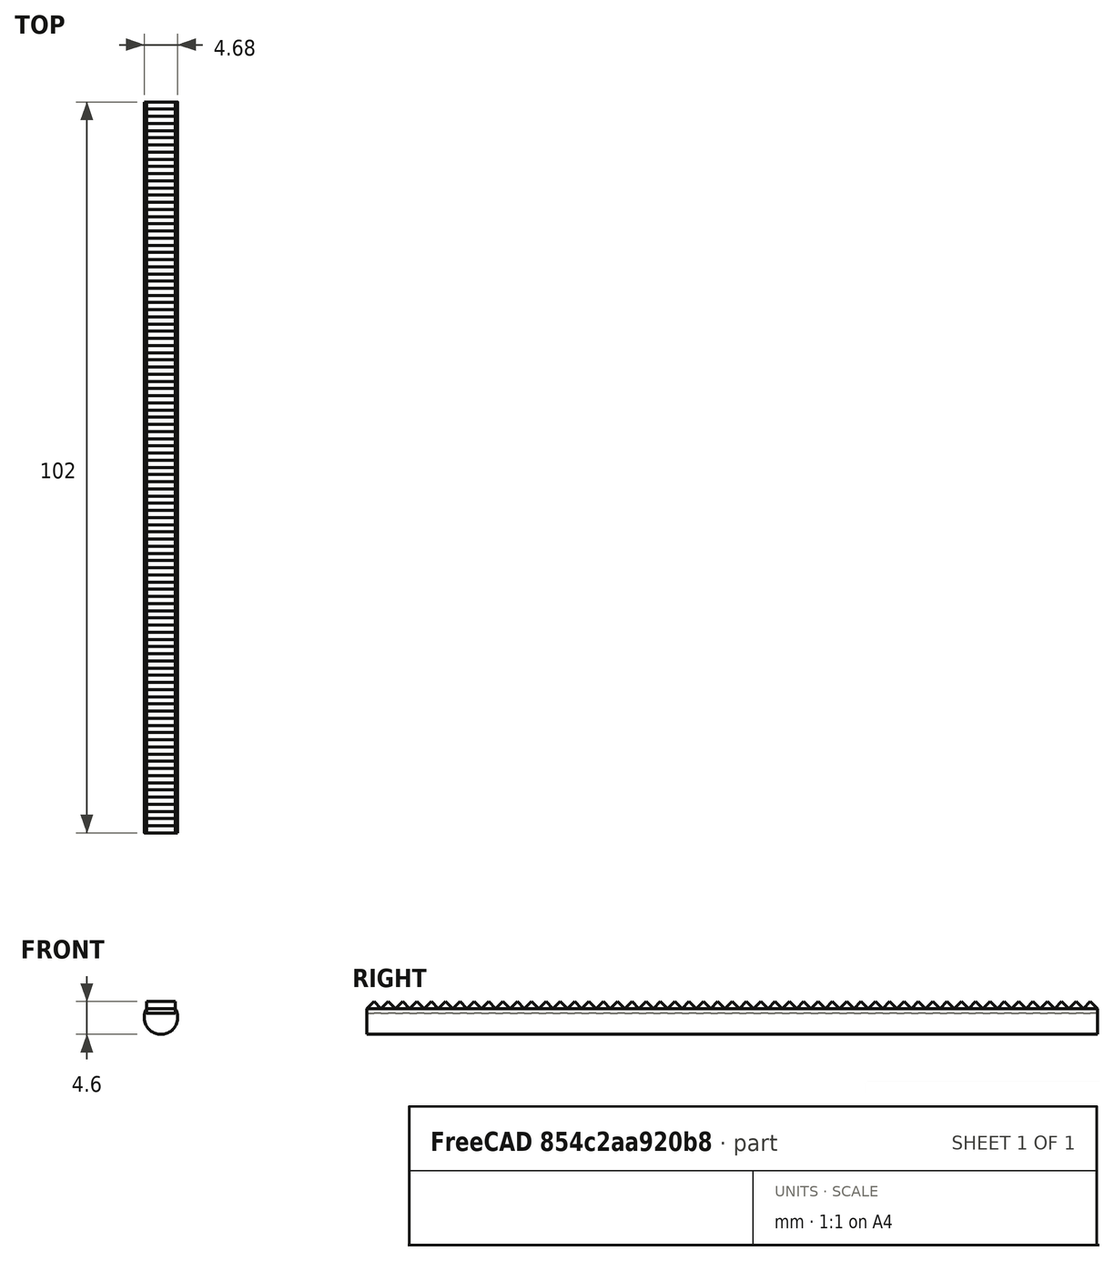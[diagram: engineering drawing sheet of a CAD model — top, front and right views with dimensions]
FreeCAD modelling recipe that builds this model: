
FCSTD DOCUMENT  (FreeCAD 0.19R)
Label: cremaillere
License: All rights reserved
LicenseURL: http://en.wikipedia.org/wiki/All_rights_reserved
objects: PartDesign::Body×3, Sketcher::SketchObject×2, PartDesign::Pad×2, PartDesign::LinearPattern×1, PartDesign::Boolean×1
note: 11 computed .brp shape members not serialized (recipe doc carries the construction recipe); baked Part::Feature solids carry a one-line shape summary decoded from their .brp

FEATURE [Sketcher::SketchObject] Sketch
  FullyConstrained = false
  MapMode = 5
  Placement = pos=(0,0,0) rot=(0.57735,0.57735,0.57735;2.0944rad)
  Support = -> [YZ_Plane]
  sketch-geometry (6):
    g0: LineSegment StartX=0 StartY=1.6622 StartZ=0 EndX=-1 EndY=0.662202 EndZ=0
    g1: LineSegment StartX=-1 StartY=0.662202 StartZ=0 EndX=-1 EndY=0 EndZ=0
    g2: LineSegment StartX=-1 StartY=0 StartZ=0 EndX=0 EndY=0 EndZ=0
    g3: LineSegment StartX=0 StartY=1.6622 StartZ=0 EndX=1 EndY=0.662202 EndZ=0
    g4: LineSegment StartX=1 StartY=0.662202 StartZ=0 EndX=1 EndY=0 EndZ=0
    g5: LineSegment StartX=1 StartY=0 StartZ=0 EndX=0 EndY=0 EndZ=0
FEATURE [PartDesign::Pad] Pad
  Direction = (1,1,1)
  Length = 4
  Length2 = 100
  Placement = pos=(0,0,0) rot=(0.57735,0.57735,0.57735;2.0944rad)
  Profile = -> Sketch
  Type = 0
FEATURE [Sketcher::SketchObject] Sketch001
  FullyConstrained = false
  MapMode = 5
  Placement = pos=(0,0,0) rot=(1,0,0;1.5708rad)
  Support = -> [XZ_Plane001]
  sketch-geometry (2):
    g0: ArcOfCircle CenterX=1.41229 CenterY=-1.20241 CenterZ=0 NormalX=0 NormalY=0 NormalZ=1 AngleXU=0 Radius=2.34134 StartAngle=2.59483 EndAngle=6.82995
    g1: LineSegment StartX=-0.587706 StartY=0.0149129 StartZ=0 EndX=3.41229 EndY=0.0149129 EndZ=0
  constraints (4):
    c: Horizontal(g1)
    c: Coincident(g1,g0)
    c: Coincident(g1,g0)
    c: Distance(g1) = 4
FEATURE [PartDesign::Pad] Pad001
  Direction = (1,1,1)
  Length = 102
  Length2 = 100
  Placement = pos=(0,0,0) rot=(1,0,0;1.5708rad)
  Profile = -> Sketch001
  Reversed = true
  Type = 0
FEATURE [PartDesign::Body] Body001
  Group = -> [Sketch001,Pad001]
  Origin = -> Origin001
  Placement = pos=(0.59,-1,0) rot=(0,0,1;0rad)
  Tip = -> Pad001
FEATURE [PartDesign::LinearPattern] LinearPattern
  BaseFeature = -> Pad
  Direction = -> Y_Axis
  Length = 100
  Occurrences = 51
  Originals = -> [Pad]
  Placement = pos=(0,0,0) rot=(0.57735,0.57735,0.57735;2.0944rad)
FEATURE [PartDesign::Body] Body
  Group = -> [Sketch,Pad,LinearPattern]
  Origin = -> Origin
  Placement = pos=(0,0,-0.6) rot=(0,0,1;0rad)
  Tip = -> LinearPattern
FEATURE [PartDesign::Boolean] Boolean
  Group = -> [Body,Body001]
  Type = 0
FEATURE [PartDesign::Body] Body002  label="piece"
  Group = -> [Boolean]
  Origin = -> Origin002
  Tip = -> Boolean
